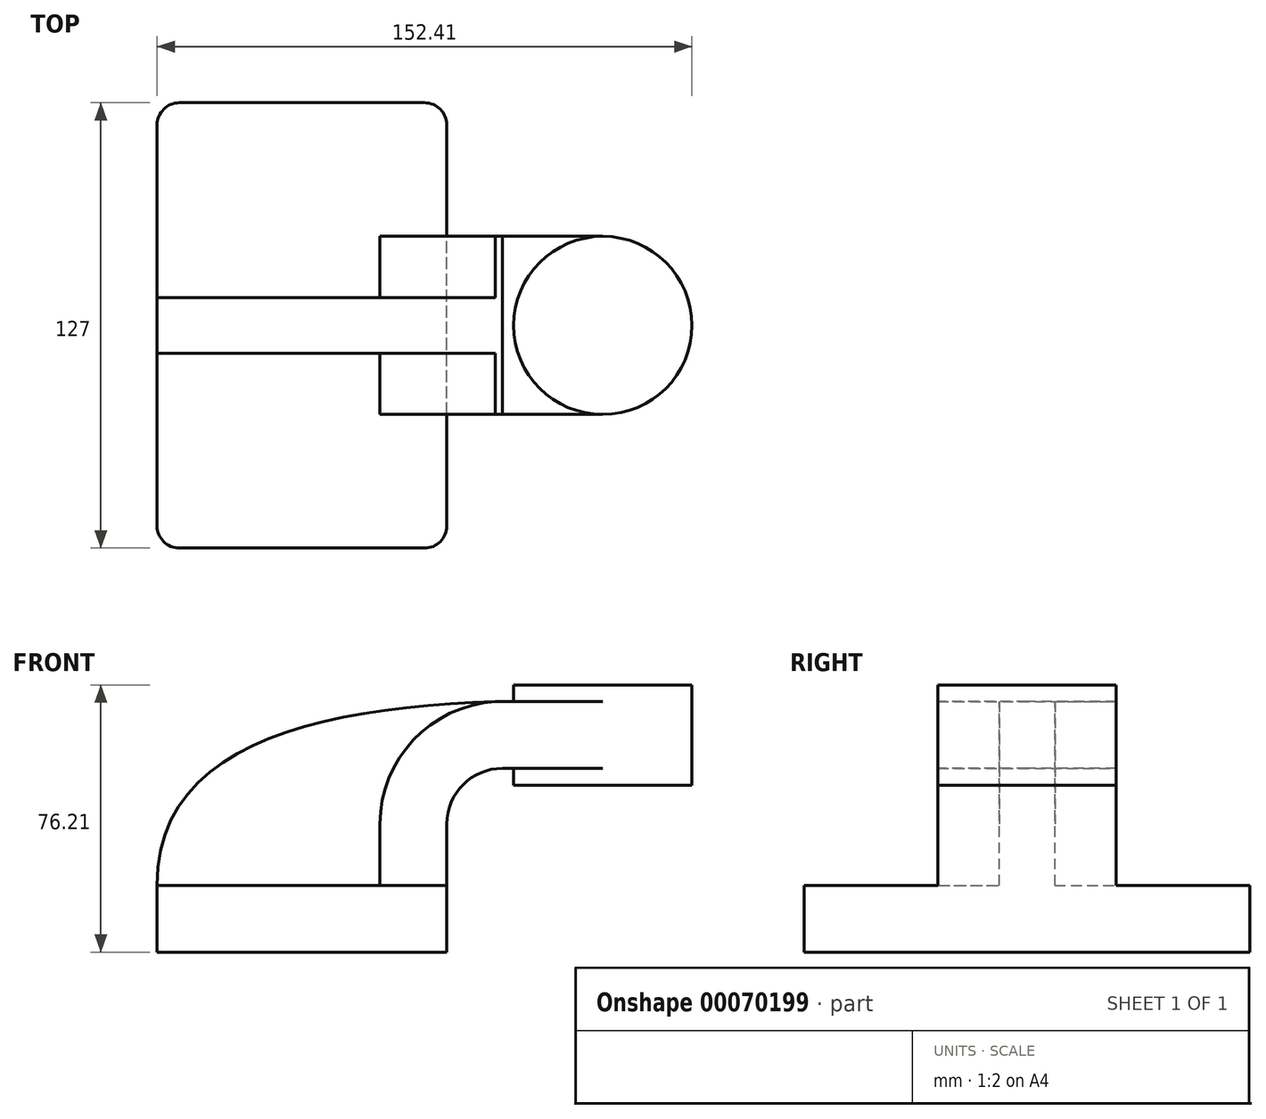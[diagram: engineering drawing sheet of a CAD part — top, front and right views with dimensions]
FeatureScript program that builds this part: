
annotation { "Feature Type Name" : "Feature", "Feature Type Description" : "" }
export const myFeature = defineFeature(function(context is Context, id is Id, definition is map)
    precondition{}
    {
        {
            var Q0;
            Q0=qCreatedBy(makeId("Front.planeOp"),FACE);
            var sketch = newSketch(context, id + "F0", { "sketchPlane" : qUnion([Q0])});
            skLineSegment(sketch, "E0.rect.bottom", {"start": v(-41.28, -9.53) * mm, "end": v(41.28, -9.53) * mm});
            skLineSegment(sketch, "E0.rect.top", {"start": v(-41.28, 9.53) * mm, "end": v(41.28, 9.53) * mm});
            skLineSegment(sketch, "E0.rect.left", {"start": v(-41.28, -9.53) * mm, "end": v(-41.28, 9.53) * mm});
            skLineSegment(sketch, "E0.rect.right", {"start": v(41.28, -9.53) * mm, "end": v(41.28, 9.53) * mm});
            skPoint(sketch, "E0.rect.middle", {"position": v(0, 0) * mm});
            skLineSegment(sketch, "E1.rect.bottom", {"start": v(60.33, 38.1) * mm, "end": v(111.13, 38.1) * mm});
            skLineSegment(sketch, "E1.rect.top", {"start": v(60.32, 66.67) * mm, "end": v(111.13, 66.67) * mm});
            skLineSegment(sketch, "E1.rect.left", {"start": v(60.33, 38.1) * mm, "end": v(60.33, 66.68) * mm});
            skLineSegment(sketch, "E1.rect.right", {"start": v(111.13, 38.1) * mm, "end": v(111.13, 66.68) * mm});
            skPoint(sketch, "E1.rect.middle", {"position": v(85.72, 52.39) * mm});
            skLineSegment(sketch, "E2", {"start": v(41.28, 9.52) * mm, "end": v(41.28, 27) * mm});
            skArc(sketch, "E3", {"start": v(41.27, 27) * mm, "mid": v(45.92, 38.23) * mm, "end": v(57.15, 42.88) * mm});
            skLineSegment(sketch, "E4", {"start": v(57.15, 42.88) * mm, "end": v(85.72, 42.88) * mm});
            skLineSegment(sketch, "E5.0", {"start": v(57.15, 61.93) * mm, "end": v(85.72, 61.93) * mm});
            skArc(sketch, "E5.1", {"start": v(22.23, 27) * mm, "mid": v(32.45, 51.7) * mm, "end": v(57.15, 61.93) * mm});
            skLineSegment(sketch, "E5.2", {"start": v(22.22, 9.52) * mm, "end": v(22.22, 27) * mm});
            skLineSegment(sketch, "E6", {"start": v(85.72, 42.88) * mm, "end": v(85.72, 38.1) * mm});
            skLineSegment(sketch, "E7", {"start": v(85.72, 38.1) * mm, "end": v(85.72, 66.67) * mm});
            skFitSpline(sketch, "E8", {"points": [v(-41.28, 9.53) * mm, v(57.15, 61.93) * mm], "startDerivative": vector(-0.57, 123.9) * mm, "endDerivative": vector(150.92, 4.12) * mm});
            skSolve(sketch);
        }
        {
            var Q0;
            Q0=makeQuery(id+"F0.imprint","IMPRINT",FACE,{"disambiguationData":[TD([[makeQuery(id+"F0.imprint","IMPRINT",EDGE,{"derivedFrom":sQuery(id+"F0.wireOp",EDGE,"E0.rect.bottom")}),1.0]])]});
            extrude(context, id + "F1", {"entities" : qUnion([Q0]), "endBound" : BoundingType.SYMMETRIC, "depth" : 127 * mm});
        }
        {
            var Q0;
            {var subQ1=sQuery(id+"F0.wireOp",EDGE,"E2");Q0=makeQuery(id+"F0.imprint","IMPRINT",FACE,{"disambiguationData":[TD([[makeQuery(id+"F0.imprint","IMPRINT",EDGE,{"derivedFrom":subQ1}),1.0]])]});}
            var Q1;
            {var subQ0=sQuery(id+"F0.wireOp",EDGE,"E4");var subQ1=sQuery(id+"F0.wireOp",EDGE,"E1.rect.left");var subQ2=makeQuery(id+"F0.imprint","INTERSECT",VERTEX,{"derivedFrom":[subQ1,subQ0]});Q1=makeQuery(id+"F0.imprint","IMPRINT",FACE,{"disambiguationData":[TD([[makeQuery(id+"F0.imprint","IMPRINT",EDGE,{"disambiguationData":[TD([[subQ2,-1.0]])],"derivedFrom":subQ1}),-1.0]])]});}
            extrude(context, id + "F2", {"entities" : qUnion([Q0, Q1]), "operationType" : NewBodyOperationType.ADD, "endBound" : BoundingType.SYMMETRIC, "depth" : 50.8 * mm});
        }
        {
            var Q0;
            {var subQ3=sQuery(id+"F0.wireOp",EDGE,"E5.2");Q0=makeQuery(id+"F0.imprint","IMPRINT",FACE,{"disambiguationData":[TD([[makeQuery(id+"F0.imprint","IMPRINT",EDGE,{"derivedFrom":subQ3}),1.0]])]});}
            extrude(context, id + "F3", {"entities" : qUnion([Q0]), "operationType" : NewBodyOperationType.ADD, "endBound" : BoundingType.SYMMETRIC, "depth" : 15.88 * mm});
        }
        {
            var Q0;
            {var subQ0=sQuery(id+"F0.wireOp",EDGE,"E1.rect.right");Q0=makeQuery(id+"F0.imprint","IMPRINT",FACE,{"disambiguationData":[TD([[makeQuery(id+"F0.imprint","IMPRINT",EDGE,{"derivedFrom":subQ0}),1.0]])]});}
            var Q1;
            Q1=sQuery(id+"F0.wireOp",EDGE,"E7");
            revolve(context, id + "F4", {"operationType" : NewBodyOperationType.ADD, "entities" : qUnion([Q0]), "axis" : qUnion([Q1]), "revolveType" : RevolveType.FULL});
        }
        {
            var Q0;
            Q0=makeQuery(id+"F1.opExtrude","CAP_EDGE",EDGE,{"disambiguationData":[OSD([sQuery(id+"F0.wireOp",EDGE,"E0.rect.left")])],"isStart":false});
            var Q1;
            Q1=makeQuery(id+"F1.opExtrude","CAP_EDGE",EDGE,{"disambiguationData":[OSD([sQuery(id+"F0.wireOp",EDGE,"E0.rect.right")])],"isStart":false});
            var Q2;
            Q2=makeQuery(id+"F1.opExtrude","CAP_EDGE",EDGE,{"disambiguationData":[OSD([sQuery(id+"F0.wireOp",EDGE,"E0.rect.right")])],"isStart":true});
            var Q3;
            Q3=makeQuery(id+"F1.opExtrude","CAP_EDGE",EDGE,{"disambiguationData":[OSD([sQuery(id+"F0.wireOp",EDGE,"E0.rect.left")])],"isStart":true});
            fillet(context, id + "F5", {"entities" : qUnion([Q0, Q1, Q2, Q3]), "radius" : 6.35 * mm, "tangentPropagation" : true, "allowEdgeOverflow" : false});
        }
    });
